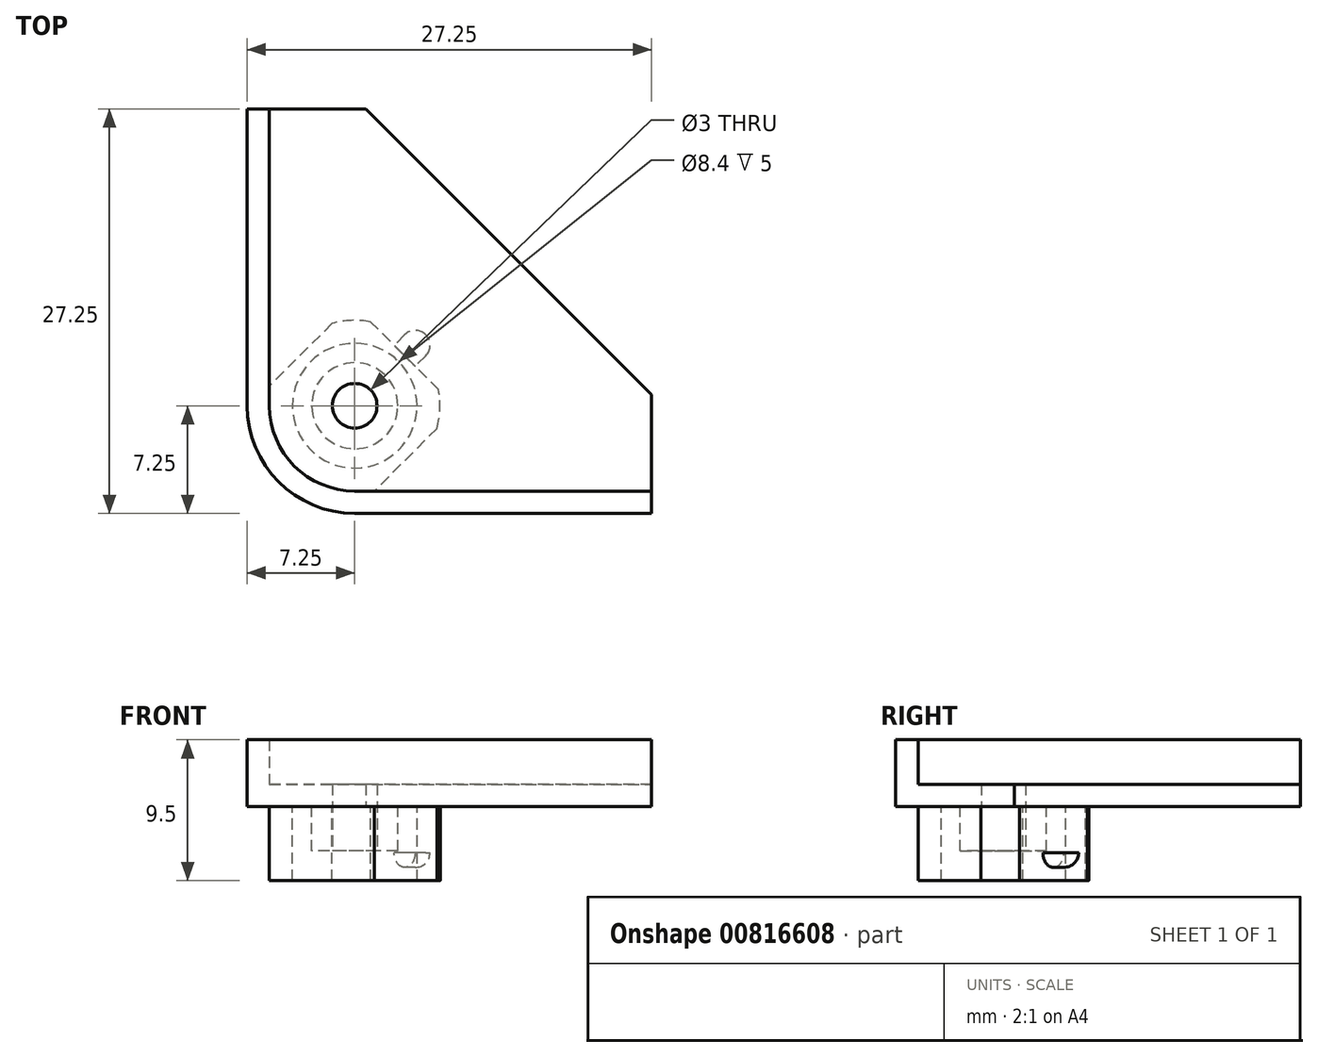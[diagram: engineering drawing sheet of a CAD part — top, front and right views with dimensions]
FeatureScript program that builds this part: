
annotation { "Feature Type Name" : "Feature", "Feature Type Description" : "" }
export const myFeature = defineFeature(function(context is Context, id is Id, definition is map)
    precondition{}
    {
        {
            var Q0;
            Q0=qCreatedBy(makeId("Top.planeOp"),FACE);
            var sketch = newSketch(context, id + "F0", { "sketchPlane" : qUnion([Q0])});
            skLineSegment(sketch, "E0", {"start": v(0, -5.75) * mm, "end": v(0, 20) * mm, "construction": true});
            skPoint(sketch, "E0.endSnap0", {"position": v(0, 35) * mm});
            skCircle(sketch, "E1", {"center": v(0, 0) * mm, "radius": 1.5 * mm});
            skCircle(sketch, "E2", {"center": v(0, 0) * mm, "radius": 2.9 * mm});
            skCircle(sketch, "E3", {"center": v(0, 0) * mm, "radius": 4.2 * mm});
            skArc(sketch, "E4", {"start": v(5.54, -1.53) * mm, "mid": v(4.07, 4.07) * mm, "end": v(-1.53, 5.54) * mm});
            skLineSegment(sketch, "E5", {"start": v(0, -5.75) * mm, "end": v(20, -5.75) * mm});
            skLineSegment(sketch, "E6", {"start": v(20, -5.75) * mm, "end": v(20, 0.75) * mm});
            skLineSegment(sketch, "E7", {"start": v(20, 0.75) * mm, "end": v(0.75, 20) * mm});
            skLineSegment(sketch, "E8", {"start": v(0.75, 20) * mm, "end": v(-5.75, 20) * mm});
            skLineSegment(sketch, "E9", {"start": v(-5.75, 20) * mm, "end": v(-5.75, 0) * mm});
            skPoint(sketch, "E10.orphan", {"position": v(0, -42.23) * mm});
            skPoint(sketch, "E11.trimOffspring.end.orphan", {"position": v(0, 43.86) * mm});
            skPoint(sketch, "E12.orphan", {"position": v(25, 35) * mm});
            skPoint(sketch, "E13.end.orphan", {"position": v(-25, 35) * mm});
            skPoint(sketch, "E14.end.orphan", {"position": v(-25, -35) * mm});
            skPoint(sketch, "E14.start.orphan", {"position": v(25, -35) * mm});
            skPoint(sketch, "E15.orphan", {"position": v(30, 0) * mm});
            skLineSegment(sketch, "E16.left", {"start": v(-1.53, 5.54) * mm, "end": v(-5.75, 1.32) * mm});
            skLineSegment(sketch, "E16.right", {"start": v(5.54, -1.53) * mm, "end": v(1.32, -5.75) * mm});
            skLineSegment(sketch, "E17.0", {"start": v(1.41, 8.49) * mm, "end": v(8.49, 1.41) * mm, "construction": true});
            skLineSegment(sketch, "E17.1", {"start": v(8.49, 1.41) * mm, "end": v(8.49, 1.41) * mm});
            skLineSegment(sketch, "E18", {"start": v(0, 0) * mm, "end": v(10.37, 10.38) * mm, "construction": true});
            skPoint(sketch, "E16.top.start.orphan", {"position": v(-8.49, -1.41) * mm});
            skPoint(sketch, "E19.orphan", {"position": v(-1.41, -8.49) * mm});
            skArc(sketch, "E20.trimOffspring", {"start": v(-5.75, 0) * mm, "mid": v(-4.07, -4.07) * mm, "end": v(0, -5.75) * mm});
            skSolve(sketch);
        }
        {
            var Q0;
            Q0 = qSketchRegion(id + "F0", true);
            var Q1;
            Q1=makeQuery(id+"F0.imprint","IMPRINT",FACE,{"disambiguationData":[TD([[makeQuery(id+"F0.imprint","IMPRINT",EDGE,{"derivedFrom":sQuery(id+"F0.wireOp",EDGE,"E2")}),-1.0]])]});
            var Q2;
            Q2=makeQuery(id+"F0.imprint","IMPRINT",FACE,{"disambiguationData":[TD([[makeQuery(id+"F0.imprint","IMPRINT",EDGE,{"derivedFrom":sQuery(id+"F0.wireOp",EDGE,"E1")}),-1.0]])]});
            extrude(context, id + "F1", {"entities" : qUnion([Q0, Q1, Q2]), "depth" : 1.5 * mm, "offsetDistance" : 25 * mm});
        }
        {
            var Q0;
            Q0=makeQuery(id+"F0.imprint","IMPRINT",FACE,{"disambiguationData":[TD([[makeQuery(id+"F0.imprint","IMPRINT",EDGE,{"derivedFrom":sQuery(id+"F0.wireOp",EDGE,"E3")}),-1.0]])]});
            extrude(context, id + "F2", {"entities" : qUnion([Q0]), "operationType" : NewBodyOperationType.ADD, "depth" : -5 * mm, "offsetDistance" : 25 * mm});
        }
        {
            var Q0;
            Q0=makeQuery(id+"F0.imprint","IMPRINT",FACE,{"disambiguationData":[TD([[makeQuery(id+"F0.imprint","IMPRINT",EDGE,{"derivedFrom":sQuery(id+"F0.wireOp",EDGE,"E1")}),-1.0]])]});
            extrude(context, id + "F3", {"entities" : qUnion([Q0]), "operationType" : NewBodyOperationType.ADD, "depth" : -3 * mm, "offsetDistance" : 25 * mm});
        }
        {
            var Q0;
            Q0=qCreatedBy(makeId("Top.planeOp"),FACE);
            var sketch = newSketch(context, id + "F4", { "sketchPlane" : qUnion([Q0])});
            skArc(sketch, "E21", {"start": v(-5.75, 0) * mm, "mid": v(-4.07, -4.07) * mm, "end": v(0, -5.75) * mm});
            skLineSegment(sketch, "E22", {"start": v(0, -5.75) * mm, "end": v(20, -5.75) * mm});
            skLineSegment(sketch, "E23", {"start": v(-5.75, 0) * mm, "end": v(-5.75, 20) * mm});
            skLineSegment(sketch, "E24.0", {"start": v(-7.25, 0) * mm, "end": v(-7.25, 20) * mm});
            skArc(sketch, "E24.1", {"start": v(-7.25, 0) * mm, "mid": v(-5.13, -5.13) * mm, "end": v(0, -7.25) * mm});
            skLineSegment(sketch, "E24.2", {"start": v(0, -7.25) * mm, "end": v(20, -7.25) * mm});
            skLineSegment(sketch, "E25", {"start": v(-7.25, 20) * mm, "end": v(-5.75, 20) * mm});
            skLineSegment(sketch, "E26", {"start": v(20, -7.25) * mm, "end": v(20, -5.75) * mm});
            skSolve(sketch);
        }
        {
            var Q0;
            Q0 = qSketchRegion(id + "F4", true);
            extrude(context, id + "F5", {"entities" : qUnion([Q0]), "operationType" : NewBodyOperationType.ADD, "depth" : 4.5 * mm, "offsetDistance" : 25 * mm});
        }
        {
            var Q0;
            Q0=makeQuery(id+"F2.opExtrude","SWEPT_FACE",FACE,{"disambiguationData":[OSD([sQuery(id+"F0.wireOp",EDGE,"E16.left")])]});
            cPlane(context, id + "F6", {"entities" : qUnion([Q0]), "cplaneType" : CPlaneType.OFFSET, "offset" : 0 * mm, "width" : 150 * mm, "height" : 150 * mm});
        }
        {
            var Q0;
            Q0=qCreatedBy(id+"F6.planeOp",FACE);
            var sketch = newSketch(context, id + "F7", { "sketchPlane" : qUnion([Q0])});
            skLineSegment(sketch, "E27.bottom", {"start": v(-5.76, 0) * mm, "end": v(-4.76, 0) * mm});
            skLineSegment(sketch, "E27.top", {"start": v(-5.76, -5) * mm, "end": v(-4.76, -5) * mm});
            skLineSegment(sketch, "E27.left", {"start": v(-5.76, 0) * mm, "end": v(-5.76, -5) * mm});
            skLineSegment(sketch, "E27.right", {"start": v(-4.76, 0) * mm, "end": v(-4.76, -5) * mm});
            skSolve(sketch);
        }
        {
            var Q0;
            Q0 = qSketchRegion(id + "F7", true);
            extrude(context, id + "F8", {"entities" : qUnion([Q0]), "operationType" : NewBodyOperationType.REMOVE, "oppositeDirection" : true, "depth" : 10 * mm, "offsetDistance" : 25 * mm});
        }
        {
            var Q0;
            Q0=makeQuery(id+"F8.boolean.opBoolean","COPY",FACE,{"derivedFrom":makeQuery(id+"F8.opExtrude","SWEPT_FACE",FACE,{"disambiguationData":[OSD([sQuery(id+"F7.wireOp",EDGE,"E27.right")])]})});
            var sketch = newSketch(context, id + "F9", { "sketchPlane" : qUnion([Q0])});
            skCircle(sketch, "E28", {"center": v(0, -3.1) * mm, "radius": 1 * mm});
            skPoint(sketch, "E28.centerSnap0", {"position": v(0, 0) * mm});
            skPoint(sketch, "E28.centerSnap1", {"position": v(3.23, -2.5) * mm});
            skSolve(sketch);
        }
        {
            var Q0;
            Q0 = qSketchRegion(id + "F9", true);
            extrude(context, id + "F10", {"entities" : qUnion([Q0]), "operationType" : NewBodyOperationType.ADD, "depth" : 2 * mm, "offsetDistance" : 25 * mm});
        }
        {
            var Q0;
            Q0=makeQuery(id+"F10.opExtrude","CAP_EDGE",EDGE,{"disambiguationData":[OSD([sQuery(id+"F9.wireOp",EDGE,"E28")])],"isStart":false});
            fillet(context, id + "F11", {"entities" : qUnion([Q0]), "radius" : 1 * mm, "tangentPropagation" : true, "allowEdgeOverflow" : false});
        }
        {
            var Q0;
            Q0=makeQuery(id+"F8.boolean.opBoolean","COPY",FACE,{"derivedFrom":makeQuery(id+"F8.opExtrude","SWEPT_FACE",FACE,{"disambiguationData":[OSD([sQuery(id+"F7.wireOp",EDGE,"E27.right")])]})});
            var sketch = newSketch(context, id + "F12", { "sketchPlane" : qUnion([Q0])});
            skLineSegment(sketch, "E29.bottom", {"start": v(-1.15, -3.1) * mm, "end": v(1.08, -3.1) * mm});
            skLineSegment(sketch, "E29.top", {"start": v(-1.15, -1.9) * mm, "end": v(1.08, -1.9) * mm});
            skLineSegment(sketch, "E29.left", {"start": v(-1.15, -3.1) * mm, "end": v(-1.15, -1.9) * mm});
            skLineSegment(sketch, "E29.right", {"start": v(1.08, -3.1) * mm, "end": v(1.08, -1.9) * mm});
            skSolve(sketch);
        }
        {
            var Q0;
            Q0 = qSketchRegion(id + "F12", true);
            extrude(context, id + "F13", {"entities" : qUnion([Q0]), "operationType" : NewBodyOperationType.REMOVE, "oppositeDirection" : true, "depth" : -3 * mm, "offsetDistance" : 25 * mm});
        }
    });
